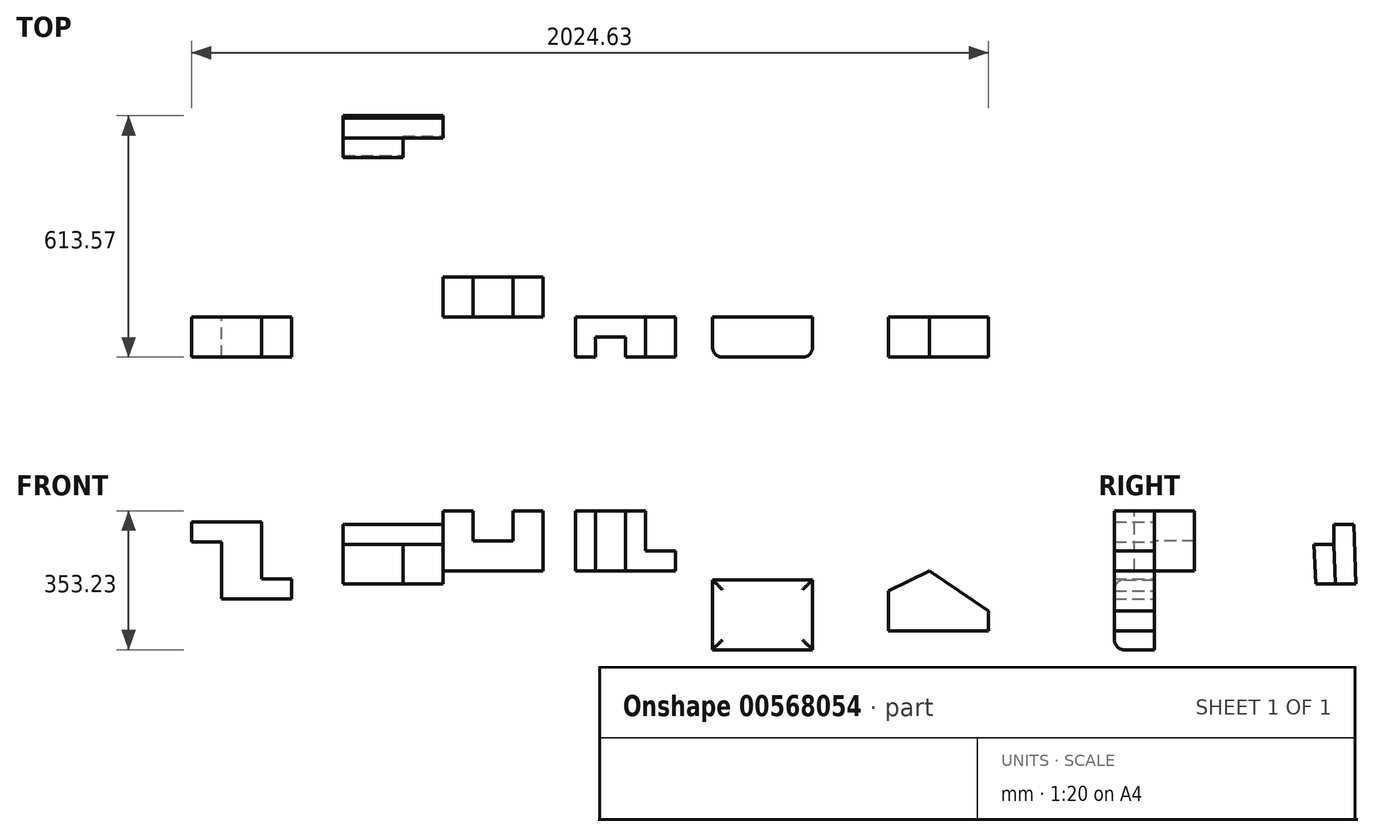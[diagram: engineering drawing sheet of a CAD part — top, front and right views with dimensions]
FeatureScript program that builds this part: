
annotation { "Feature Type Name" : "Feature", "Feature Type Description" : "" }
export const myFeature = defineFeature(function(context is Context, id is Id, definition is map)
    precondition{}
    {
        {
            var Q0;
            Q0=qCreatedBy(makeId("Front.planeOp"),FACE);
            var sketch = newSketch(context, id + "F0", { "sketchPlane" : qUnion([Q0])});
            skLineSegment(sketch, "E0", {"start": v(0, 0) * mm, "end": v(0, 152.4) * mm});
            skLineSegment(sketch, "E1", {"start": v(0, 152.4) * mm, "end": v(76.2, 152.4) * mm});
            skLineSegment(sketch, "E2", {"start": v(76.2, 152.4) * mm, "end": v(76.2, 76.2) * mm});
            skLineSegment(sketch, "E3", {"start": v(76.2, 76.2) * mm, "end": v(177.8, 76.2) * mm});
            skLineSegment(sketch, "E4", {"start": v(177.8, 76.2) * mm, "end": v(177.8, 152.4) * mm});
            skLineSegment(sketch, "E5", {"start": v(177.8, 152.4) * mm, "end": v(254, 152.4) * mm});
            skLineSegment(sketch, "E6", {"start": v(254, 152.4) * mm, "end": v(254, 0) * mm});
            skLineSegment(sketch, "E7", {"start": v(254, 0) * mm, "end": v(0, 0) * mm});
            skSolve(sketch);
        }
        {
            var Q0;
            Q0 = qSketchRegion(id + "F0", true);
            extrude(context, id + "F1", {"entities" : qUnion([Q0]), "oppositeDirection" : true, "depth" : 101.6 * mm, "offsetDistance" : 25.4 * mm});
        }
        {
            var Q0;
            Q0=qCreatedBy(makeId("Right.planeOp"),FACE);
            var sketch = newSketch(context, id + "F2", { "sketchPlane" : qUnion([Q0])});
            skLineSegment(sketch, "E8", {"start": v(410.37, -34.16) * mm, "end": v(511.97, -34.16) * mm});
            skLineSegment(sketch, "E9", {"start": v(511.97, -34.16) * mm, "end": v(506.1, 118.13) * mm});
            skLineSegment(sketch, "E10", {"start": v(506.1, 118.13) * mm, "end": v(455.3, 118.13) * mm});
            skLineSegment(sketch, "E11", {"start": v(455.3, 118.13) * mm, "end": v(455.3, 67.33) * mm});
            skLineSegment(sketch, "E12", {"start": v(455.3, 67.33) * mm, "end": v(405.58, 67.33) * mm});
            skLineSegment(sketch, "E13", {"start": v(405.58, 67.33) * mm, "end": v(410.37, -34.16) * mm});
            skSolve(sketch);
        }
        {
            var Q0;
            Q0 = qSketchRegion(id + "F2", true);
            extrude(context, id + "F3", {"entities" : qUnion([Q0]), "oppositeDirection" : true, "depth" : 254 * mm, "offsetDistance" : 25.4 * mm});
        }
        {
            var Q0;
            Q0=makeQuery(id+"F3.opExtrude","CAP_FACE",FACE,{"disambiguationData":[OSD([sQuery(id+"F2.wireOp",EDGE,"E8"),sQuery(id+"F2.wireOp",EDGE,"E9"),sQuery(id+"F2.wireOp",EDGE,"E10"),sQuery(id+"F2.wireOp",EDGE,"E11"),sQuery(id+"F2.wireOp",EDGE,"E12"),sQuery(id+"F2.wireOp",EDGE,"E13")])],"isStart":true});
            var sketch = newSketch(context, id + "F4", { "sketchPlane" : qUnion([Q0])});
            skLineSegment(sketch, "E14", {"start": v(455.3, 67.33) * mm, "end": v(460.1, -34.16) * mm});
            skLineSegment(sketch, "E15", {"start": v(460.1, -34.16) * mm, "end": v(410.37, -34.16) * mm});
            skLineSegment(sketch, "E16", {"start": v(410.37, -34.16) * mm, "end": v(405.58, 67.33) * mm});
            skLineSegment(sketch, "E17", {"start": v(405.58, 67.33) * mm, "end": v(455.3, 67.33) * mm});
            skSolve(sketch);
        }
        {
            var Q0;
            Q0=makeQuery(id+"F4.imprint","IMPRINT",FACE,{"disambiguationData":[TD([[makeQuery(id+"F4.imprint","IMPRINT",EDGE,{"derivedFrom":sQuery(id+"F4.wireOp",EDGE,"E14")}),-1.0]])]});
            extrude(context, id + "F5", {"entities" : qUnion([Q0]), "operationType" : NewBodyOperationType.REMOVE, "oppositeDirection" : true, "depth" : 101.6 * mm, "offsetDistance" : 25.4 * mm});
        }
        {
            var Q0;
            Q0=qCreatedBy(makeId("Front.planeOp"),FACE);
            var sketch = newSketch(context, id + "F6", { "sketchPlane" : qUnion([Q0])});
            skLineSegment(sketch, "E18", {"start": v(336.14, 0) * mm, "end": v(336.14, 152.4) * mm});
            skLineSegment(sketch, "E19", {"start": v(336.14, 152.4) * mm, "end": v(513.94, 152.4) * mm});
            skLineSegment(sketch, "E20", {"start": v(513.94, 152.4) * mm, "end": v(513.94, 50.8) * mm});
            skLineSegment(sketch, "E21", {"start": v(513.94, 50.8) * mm, "end": v(590.14, 50.8) * mm});
            skLineSegment(sketch, "E22", {"start": v(590.14, 50.8) * mm, "end": v(590.14, 0) * mm});
            skLineSegment(sketch, "E23", {"start": v(590.14, 0) * mm, "end": v(336.14, 0) * mm});
            skSolve(sketch);
        }
        {
            var Q0;
            Q0=makeQuery(id+"F6.imprint","IMPRINT",FACE,{"disambiguationData":[TD([[makeQuery(id+"F6.imprint","IMPRINT",EDGE,{"derivedFrom":sQuery(id+"F6.wireOp",EDGE,"E18")}),-1.0]])]});
            extrude(context, id + "F7", {"entities" : qUnion([Q0]), "depth" : 101.6 * mm, "offsetDistance" : 25.4 * mm});
        }
        {
            var Q0;
            Q0=makeQuery(id+"F7.opExtrude","SWEPT_FACE",FACE,{"disambiguationData":[OSD([sQuery(id+"F6.wireOp",EDGE,"E19")])]});
            var sketch = newSketch(context, id + "F8", { "sketchPlane" : qUnion([Q0])});
            skLineSegment(sketch, "E24", {"start": v(463.14, -101.6) * mm, "end": v(463.14, -50.8) * mm});
            skLineSegment(sketch, "E25", {"start": v(463.14, -50.8) * mm, "end": v(386.94, -50.8) * mm});
            skLineSegment(sketch, "E26", {"start": v(386.94, -50.8) * mm, "end": v(386.94, -101.6) * mm});
            skSolve(sketch);
        }
        {
            var Q0;
            Q0 = qSketchRegion(id + "F8", true);
            var Q1;
            {var subQ0=sQuery(id+"F8.wireOp",EDGE,"E24");Q1=makeQuery(id+"F8.imprint","IMPRINT",FACE,{"disambiguationData":[TD([[makeQuery(id+"F8.imprint","IMPRINT",EDGE,{"derivedFrom":subQ0}),1.0]])]});}
            extrude(context, id + "F9", {"entities" : qUnion([Q0, Q1]), "operationType" : NewBodyOperationType.REMOVE, "oppositeDirection" : true, "depth" : 152.4 * mm, "offsetDistance" : 25.4 * mm});
        }
        {
            var Q0;
            Q0=qCreatedBy(makeId("Front.planeOp"),FACE);
            var sketch = newSketch(context, id + "F10", { "sketchPlane" : qUnion([Q0])});
            skLineSegment(sketch, "E27", {"start": v(-639.65, 124.15) * mm, "end": v(-461.85, 124.15) * mm});
            skLineSegment(sketch, "E28", {"start": v(-461.85, 124.15) * mm, "end": v(-461.85, -20.46) * mm});
            skLineSegment(sketch, "E29", {"start": v(-461.85, -20.46) * mm, "end": v(-385.65, -20.46) * mm});
            skLineSegment(sketch, "E30", {"start": v(-385.65, -20.46) * mm, "end": v(-385.65, -71.26) * mm});
            skLineSegment(sketch, "E31", {"start": v(-385.65, -71.26) * mm, "end": v(-563.45, -71.26) * mm});
            skLineSegment(sketch, "E32", {"start": v(-563.45, -71.26) * mm, "end": v(-563.45, 73.35) * mm});
            skLineSegment(sketch, "E33", {"start": v(-563.45, 73.35) * mm, "end": v(-639.65, 73.35) * mm});
            skLineSegment(sketch, "E34", {"start": v(-639.65, 73.35) * mm, "end": v(-639.65, 124.15) * mm});
            skSolve(sketch);
        }
        {
            var Q0;
            Q0=makeQuery(id+"F10.imprint","IMPRINT",FACE,{"disambiguationData":[TD([[makeQuery(id+"F10.imprint","IMPRINT",EDGE,{"derivedFrom":sQuery(id+"F10.wireOp",EDGE,"E27")}),-1.0]])]});
            extrude(context, id + "F11", {"entities" : qUnion([Q0]), "depth" : 101.6 * mm, "offsetDistance" : 25.4 * mm});
        }
        {
            var Q0;
            Q0=qCreatedBy(makeId("Front.planeOp"),FACE);
            var sketch = newSketch(context, id + "F12", { "sketchPlane" : qUnion([Q0])});
            skLineSegment(sketch, "E35", {"start": v(1130.98, -152.4) * mm, "end": v(1384.98, -152.4) * mm});
            skLineSegment(sketch, "E36", {"start": v(1384.98, -152.4) * mm, "end": v(1384.98, -101.6) * mm});
            skLineSegment(sketch, "E37", {"start": v(1384.98, -101.6) * mm, "end": v(1235.19, 0) * mm});
            skLineSegment(sketch, "E38", {"start": v(1235.19, 0) * mm, "end": v(1130.98, -50.8) * mm});
            skLineSegment(sketch, "E39", {"start": v(1130.98, -50.8) * mm, "end": v(1130.98, -152.4) * mm});
            skLineSegment(sketch, "E40", {"start": v(1235.19, 0) * mm, "end": v(1235.19, -152.4) * mm});
            skPoint(sketch, "E40.endSnap0", {"position": v(1257.98, -152.4) * mm});
            skSolve(sketch);
        }
        {
            var Q0;
            Q0=makeQuery(id+"F12.imprint","IMPRINT",FACE,{"disambiguationData":[TD([[makeQuery(id+"F12.imprint","IMPRINT",EDGE,{"derivedFrom":sQuery(id+"F12.wireOp",EDGE,"E38")}),1.0]])]});
            var Q1;
            {var subQ0=sQuery(id+"F12.wireOp",EDGE,"E36");Q1=makeQuery(id+"F12.imprint","IMPRINT",FACE,{"disambiguationData":[TD([[makeQuery(id+"F12.imprint","IMPRINT",EDGE,{"derivedFrom":subQ0}),1.0]])]});}
            extrude(context, id + "F13", {"entities" : qUnion([Q0, Q1]), "depth" : 101.6 * mm, "offsetDistance" : 25.4 * mm});
        }
        {
            var Q0;
            Q0=qCreatedBy(makeId("Front.planeOp"),FACE);
            var sketch = newSketch(context, id + "F14", { "sketchPlane" : qUnion([Q0])});
            skLineSegment(sketch, "E41", {"start": v(684.02, -200.83) * mm, "end": v(938.02, -200.83) * mm});
            skLineSegment(sketch, "E42", {"start": v(938.02, -200.83) * mm, "end": v(938.02, -23.03) * mm});
            skLineSegment(sketch, "E43", {"start": v(938.02, -23.03) * mm, "end": v(684.02, -23.03) * mm});
            skLineSegment(sketch, "E44", {"start": v(684.02, -23.03) * mm, "end": v(684.02, -200.83) * mm});
            skSolve(sketch);
        }
        {
            var Q0;
            Q0=makeQuery(id+"F14.imprint","IMPRINT",FACE,{"disambiguationData":[TD([[makeQuery(id+"F14.imprint","IMPRINT",EDGE,{"derivedFrom":sQuery(id+"F14.wireOp",EDGE,"E41")}),1.0]])]});
            extrude(context, id + "F15", {"entities" : qUnion([Q0]), "depth" : 101.6 * mm, "offsetDistance" : 25.4 * mm});
        }
        {
            var Q0;
            Q0=makeQuery(id+"F15.opExtrude","CAP_FACE",FACE,{"disambiguationData":[OSD([sQuery(id+"F14.wireOp",EDGE,"E41"),sQuery(id+"F14.wireOp",EDGE,"E42"),sQuery(id+"F14.wireOp",EDGE,"E43"),sQuery(id+"F14.wireOp",EDGE,"E44")])],"isStart":false});
            fillet(context, id + "F16", {"entities" : qUnion([Q0]), "radius" : 25.4 * mm, "tangentPropagation" : true, "allowEdgeOverflow" : false});
        }
    });
